# Revit family: PRD_AR_SpprtRls_MEDCAREJointForCurtainRod_ZMEDC0001
name_source: partatom
category: Specialty Equipment
units: mm (PartAtom-declared; Revit-internal decimal feet)

## family parameters
Always vertical = Yes
Cut with Voids When Loaded = No
Enable Cutting in Views = No
Maintain Annotation Orientation = No
OmniClass Number = 23.20.40.11.14
OmniClass Title = Multi-Purpose Mechanical Fasteners
Part Type = Normal
Room Calculation Point = No
Round Connector Dimension = Use Diameter
Shared = No
Work Plane-Based = No

## types (1)
- ZMEDC0001
    AssetType = Fixed
    BIMObjectName = PRD_AR_ShowerCurtainRails_MEDCAREJointForCurtainRod_ZMEDC0001
    BodyMaterial = PRD_AR_Aluminium
    Category = Pr_40_30_20_77, Shower curtain rails
    Default Elevation = 0 mm  [stored 0 ft]
    Description = MEDCARE removable joint for ceiling mounting of curtain rods, made of anodised aluminium, suitable for suicide prevention, for a tensile load of approx. 30 kg, expansion bolt included.
    Diameter = 27 mm  [stored 0.0885827 ft]
    Export Type to IFC As = IfcRailingType
    Features = for ceiling mounting of curtain rods, for a tensile load of approx. 30 kg
    Height = 0 mm  [stored 0 ft]
    IfcExportAs = IfcRailingType
    IfcExportType = USERDEFINED
    IsExternal = FALSE
    Manufacturer = KWC Group Management AG
    ManufacturerName = KWC Group Management AG
    ManufacturerURL = www.kwc-professional.com
    Material = anodised aluminium
    Model = ZMEDC0001
    ModelNumber = 3600003786
    ModelReference = ZMEDC0001
    NBSDescription = Shower curtain rails
    NBSReference = 45-35-70/334
    Name = MEDCARE Joint for curtain rod ZMEDC0001
    NominalDepth = 0 mm  [stored 0 ft]
    NominalHeight = 0 mm  [stored 0 ft]
    NominalLength = 0 mm  [stored 0 ft]
    NominalWidth = 0 mm  [stored 0 ft]
    ProductInformation = http://pim.kwc.com
    Quantity = 1
    QuantityUom = piece
    Status = New
    Type IFC Predefined Type = USERDEFINED
    URL = www.kwc-professional.com
    Uniclass2015Code = Pr_40_30_20_77
    Uniclass2015Title = Shower curtain rails
    Uniclass2015Version = Products v1.36
    Version = 1

note: [stored X ft] marks values corroborated as IEEE doubles in the binary element streams (Revit-internal decimal feet)

## geometry (parser evidence)
native form markers: Sweep x5
no freeform markers — native parametric forms only
